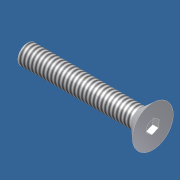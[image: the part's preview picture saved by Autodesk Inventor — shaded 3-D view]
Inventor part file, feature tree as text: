
AUTODESK INVENTOR PART (.ipt)
format: ipt  version: 2012 (Build 160160000, 160)  size: 91,648 bytes
history: native  units: in
note: dims shown in document units (in); Inventor stores cm internally (conversion verified against a paired STEP export)
features: sketch x2, revolve x1, thread x1, extrude x1
ambient origin geometry x8: Origin, YZ Plane, XZ Plane, XY Plane, X Axis, Y Axis, Z Axis, Center Point
bodies: Solid1 (feature_tree)
feature tree (5):
  revolve  "Revolution1"  [1 undecoded]
  thread  "Thread1"  [1 undecoded]
  extrude  "Extrusion1"  Depth=1.0in TaperAngle=0.0deg
  sketch  "Sketch1"  dims[d1=0.125in d2=0.161in d3=0.2655in]
  sketch  "Sketch2"  dims[d4=90.0deg d5=1.0in d6=0.0in d16=0.1562in d17=0.075in d18=0.0in d20=1.625in]
note: 2 required parameter values undecoded (feature->parameter linkage not recoverable at this tier; creation-order binding heuristic only, values carry confidence <= 0.55)